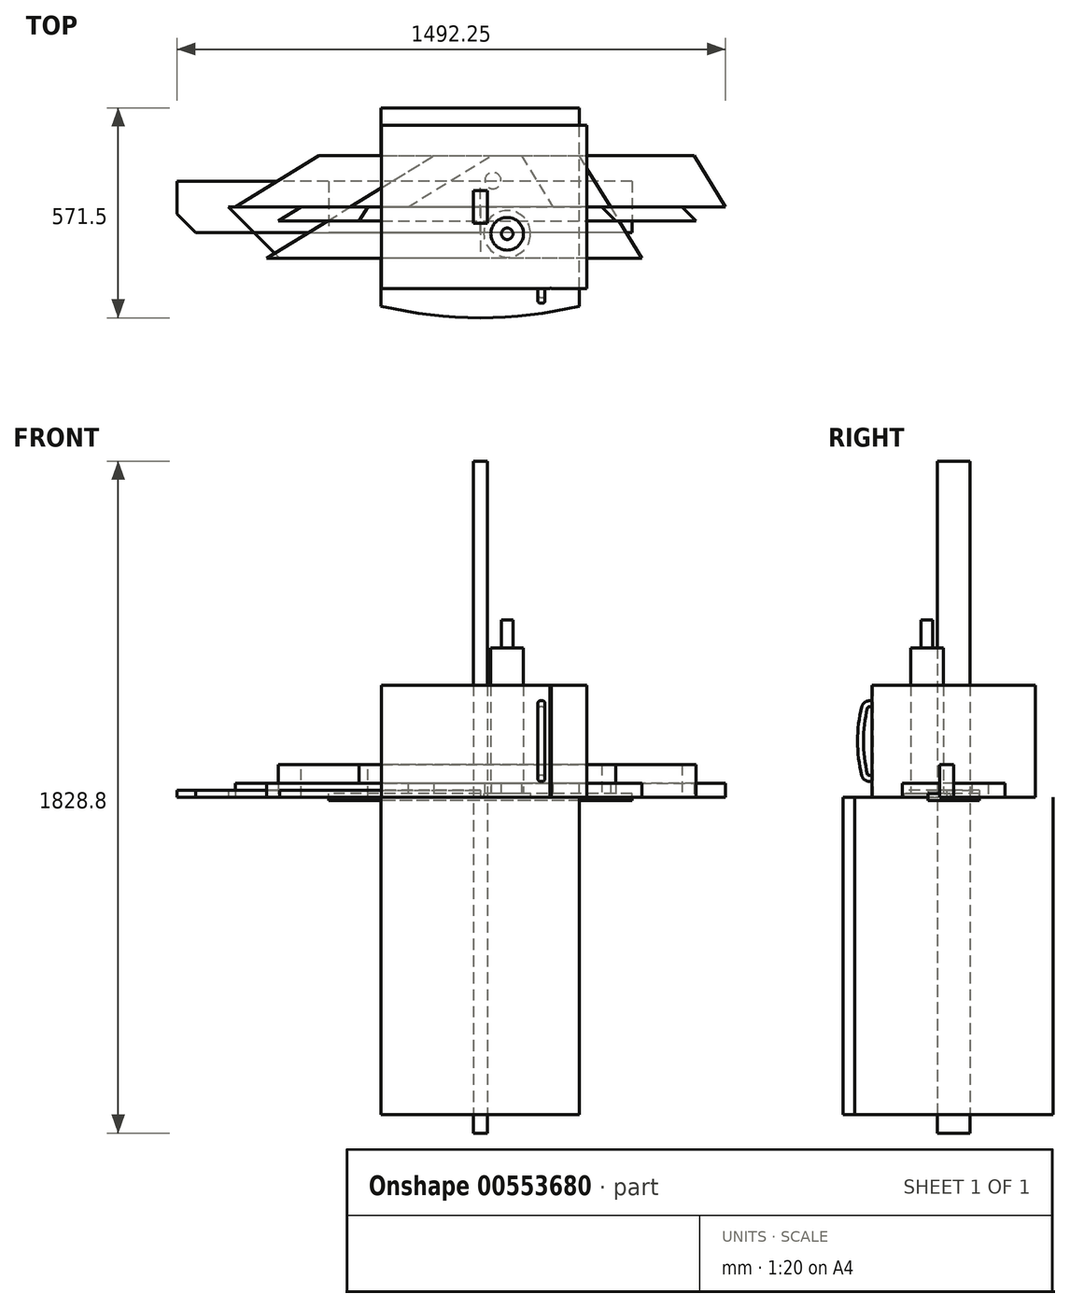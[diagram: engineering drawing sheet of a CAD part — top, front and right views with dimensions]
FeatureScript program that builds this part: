
annotation { "Feature Type Name" : "Feature", "Feature Type Description" : "" }
export const myFeature = defineFeature(function(context is Context, id is Id, definition is map)
    precondition{}
    {
        {
            var Q0;
            Q0=qCreatedBy(makeId("Top.planeOp"),FACE);
            var sketch = newSketch(context, id + "F0", { "sketchPlane" : qUnion([Q0])});
            skLineSegment(sketch, "E0.bottom", {"start": v(269.88, -269.88) * mm, "end": v(-269.88, -269.88) * mm});
            skLineSegment(sketch, "E0.top", {"start": v(269.88, 269.88) * mm, "end": v(-269.88, 269.88) * mm});
            skLineSegment(sketch, "E0.left", {"start": v(269.88, -269.88) * mm, "end": v(269.88, 269.88) * mm});
            skLineSegment(sketch, "E0.right", {"start": v(-269.88, -269.88) * mm, "end": v(-269.88, 269.88) * mm});
            skPoint(sketch, "E0.middle", {"position": v(0, 0) * mm});
            skArc(sketch, "E1", {"start": v(-269.88, -269.88) * mm, "mid": v(0, -301.62) * mm, "end": v(269.88, -269.87) * mm});
            skCircle(sketch, "E2", {"center": v(73.03, -73.03) * mm, "radius": 63.5 * mm});
            skCircle(sketch, "E3", {"center": v(73.03, -73.03) * mm, "radius": 44.45 * mm});
            skSolve(sketch);
        }
        {
            var Q0;
            Q0=makeQuery(id+"F0.imprint","IMPRINT",FACE,{"disambiguationData":[TD([[makeQuery(id+"F0.imprint","IMPRINT",EDGE,{"derivedFrom":sQuery(id+"F0.wireOp",EDGE,"E0.bottom")}),-1.0]])]});
            var Q1;
            Q1=makeQuery(id+"F0.imprint","IMPRINT",FACE,{"disambiguationData":[TD([[makeQuery(id+"F0.imprint","IMPRINT",EDGE,{"derivedFrom":sQuery(id+"F0.wireOp",EDGE,"E0.bottom")}),1.0]])]});
            var Q2;
            Q2=makeQuery(id+"F0.imprint","IMPRINT",FACE,{"disambiguationData":[TD([[makeQuery(id+"F0.imprint","IMPRINT",EDGE,{"derivedFrom":sQuery(id+"F0.wireOp",EDGE,"E2")}),1.0]])]});
            var Q3;
            Q3=makeQuery(id+"F0.imprint","IMPRINT",FACE,{"disambiguationData":[TD([[makeQuery(id+"F0.imprint","IMPRINT",EDGE,{"derivedFrom":sQuery(id+"F0.wireOp",EDGE,"E3")}),1.0]])]});
            extrude(context, id + "F1", {"entities" : qUnion([Q0, Q1, Q2, Q3]), "oppositeDirection" : true, "depth" : 863.6 * mm, "offsetDistance" : 25.4 * mm});
        }
        {
            var Q0;
            Q0=makeQuery(id+"F0.imprint","IMPRINT",FACE,{"disambiguationData":[TD([[makeQuery(id+"F0.imprint","IMPRINT",EDGE,{"derivedFrom":sQuery(id+"F0.wireOp",EDGE,"E3")}),1.0]])]});
            extrude(context, id + "F2", {"entities" : qUnion([Q0]), "operationType" : NewBodyOperationType.ADD, "depth" : 406.4 * mm, "offsetDistance" : 25.4 * mm});
        }
        {
            var Q0;
            Q0=makeQuery(id+"F0.imprint","IMPRINT",FACE,{"disambiguationData":[TD([[makeQuery(id+"F0.imprint","IMPRINT",EDGE,{"derivedFrom":sQuery(id+"F0.wireOp",EDGE,"E2")}),1.0]])]});
            extrude(context, id + "F3", {"entities" : qUnion([Q0]), "operationType" : NewBodyOperationType.ADD, "depth" : 9.52 * mm, "offsetDistance" : 25.4 * mm});
        }
        {
            var Q0;
            Q0=qCreatedBy(makeId("Right.planeOp"),FACE);
            var Q1;
            Q1=sQuery(id+"F0.wireOp",VERTEX,"E3.center");
            cPlane(context, id + "F4", {"entities" : qUnion([Q0, Q1]), "cplaneType" : CPlaneType.PLANE_POINT, "offset" : 114.3 * mm, "width" : 152.4 * mm, "height" : 152.4 * mm});
        }
        {
            var Q0;
            Q0=qCreatedBy(id+"F4.planeOp",FACE);
            var sketch = newSketch(context, id + "F5", { "sketchPlane" : qUnion([Q0])});
            skLineSegment(sketch, "E4", {"start": v(-117.48, 368.3) * mm, "end": v(-149.22, 368.3) * mm});
            skLineSegment(sketch, "E5", {"start": v(-149.22, 368.3) * mm, "end": v(-168.27, 349.25) * mm});
            skLineSegment(sketch, "E6", {"start": v(-168.27, 349.25) * mm, "end": v(-168.27, 336.55) * mm});
            skLineSegment(sketch, "E7", {"start": v(-117.48, 368.3) * mm, "end": v(-92.08, 368.3) * mm});
            skLineSegment(sketch, "E8", {"start": v(-117.48, 9.53) * mm, "end": v(-117.48, 406.4) * mm, "construction": true});
            skSolve(sketch);
        }
        {
            var Q0;
            Q0=makeQuery(id+"F2.opExtrude","CAP_FACE",FACE,{"disambiguationData":[OSD([sQuery(id+"F0.wireOp",EDGE,"E3")])],"isStart":false});
            var sketch = newSketch(context, id + "F6", { "sketchPlane" : qUnion([Q0])});
            skCircle(sketch, "E9", {"center": v(73.03, -73.03) * mm, "radius": 15.88 * mm});
            skSolve(sketch);
        }
        {
            var Q0;
            Q0=makeQuery(id+"F6.imprint","IMPRINT",FACE,{"disambiguationData":[TD([[makeQuery(id+"F6.imprint","IMPRINT",EDGE,{"derivedFrom":sQuery(id+"F6.wireOp",EDGE,"E9")}),1.0]])]});
            extrude(context, id + "F7", {"entities" : qUnion([Q0]), "operationType" : NewBodyOperationType.ADD, "depth" : 76.2 * mm, "offsetDistance" : 25.4 * mm});
        }
        {
            var Q0;
            Q0=qCreatedBy(makeId("Top.planeOp"),FACE);
            var sketch = newSketch(context, id + "F8", { "sketchPlane" : qUnion([Q0])});
            skLineSegment(sketch, "E10.bottom", {"start": v(289.8, -222.25) * mm, "end": v(-269, -222.25) * mm});
            skLineSegment(sketch, "E10.top", {"start": v(289.8, 222.25) * mm, "end": v(-269, 222.25) * mm});
            skLineSegment(sketch, "E10.left", {"start": v(289.8, -222.25) * mm, "end": v(289.8, 222.25) * mm});
            skLineSegment(sketch, "E10.right", {"start": v(-269, -222.25) * mm, "end": v(-269, 222.25) * mm});
            skPoint(sketch, "E10.middle", {"position": v(10.4, 0) * mm});
            skSolve(sketch);
        }
        {
            var Q0;
            Q0=makeQuery(id+"F8.imprint","IMPRINT",FACE,{"disambiguationData":[TD([[makeQuery(id+"F8.imprint","IMPRINT",EDGE,{"derivedFrom":sQuery(id+"F8.wireOp",EDGE,"E10.bottom")}),-1.0]])]});
            extrude(context, id + "F9", {"entities" : qUnion([Q0]), "depth" : 304.8 * mm, "offsetDistance" : 25.4 * mm});
        }
        {
            var Q0;
            Q0=makeQuery(id+"F9.opExtrude","SWEPT_FACE",FACE,{"disambiguationData":[OSD([sQuery(id+"F8.wireOp",EDGE,"E10.bottom")])]});
            var sketch = newSketch(context, id + "F10", { "sketchPlane" : qUnion([Q0])});
            skLineSegment(sketch, "E11", {"start": v(165.97, 254) * mm, "end": v(165.97, 50.8) * mm, "construction": true});
            skLineSegment(sketch, "E12.bottom", {"start": v(169.15, 246.06) * mm, "end": v(162.8, 246.06) * mm});
            skLineSegment(sketch, "E12.top", {"start": v(169.15, 261.94) * mm, "end": v(162.8, 261.94) * mm});
            skLineSegment(sketch, "E12.left", {"start": v(175.5, 252.41) * mm, "end": v(175.5, 255.59) * mm});
            skLineSegment(sketch, "E12.right", {"start": v(156.45, 252.41) * mm, "end": v(156.45, 255.59) * mm});
            skPoint(sketch, "E12.middle", {"position": v(165.97, 254) * mm});
            skPoint(sketch, "E13.visualSharp", {"position": v(156.45, 261.94) * mm});
            skArc(sketch, "E13.filletArc", {"start": v(162.8, 261.94) * mm, "mid": v(158.3, 260.08) * mm, "end": v(156.45, 255.59) * mm});
            skPoint(sketch, "E14.visualSharp", {"position": v(156.45, 246.06) * mm});
            skArc(sketch, "E14.filletArc", {"start": v(156.45, 252.41) * mm, "mid": v(158.3, 247.92) * mm, "end": v(162.8, 246.06) * mm});
            skPoint(sketch, "E15.visualSharp", {"position": v(175.5, 246.06) * mm});
            skArc(sketch, "E15.filletArc", {"start": v(169.15, 246.06) * mm, "mid": v(173.64, 247.92) * mm, "end": v(175.5, 252.41) * mm});
            skPoint(sketch, "E16.visualSharp", {"position": v(175.5, 261.94) * mm});
            skArc(sketch, "E16.filletArc", {"start": v(175.5, 255.59) * mm, "mid": v(173.64, 260.08) * mm, "end": v(169.15, 261.94) * mm});
            skSolve(sketch);
        }
        {
            var Q0;
            Q0=qCreatedBy(makeId("Right.planeOp"),FACE);
            cPlane(context, id + "F11", {"entities" : qUnion([Q0]), "cplaneType" : CPlaneType.OFFSET, "offset" : 161.92 * mm, "width" : 152.4 * mm, "height" : 152.4 * mm});
        }
        {
            var Q0;
            Q0=qCreatedBy(id+"F11.planeOp",FACE);
            var sketch = newSketch(context, id + "F12", { "sketchPlane" : qUnion([Q0])});
            skLineSegment(sketch, "E17.0", {"start": v(-222.25, 254) * mm, "end": v(-222.25, 50.8) * mm, "construction": true});
            skLineSegment(sketch, "E18", {"start": v(-222.25, 254) * mm, "end": v(-230.4, 254) * mm});
            skLineSegment(sketch, "E19", {"start": v(-230.4, 50.8) * mm, "end": v(-222.25, 50.8) * mm});
            skArc(sketch, "E20", {"start": v(-242.73, 244.37) * mm, "mid": v(-254, 152.4) * mm, "end": v(-242.73, 60.43) * mm});
            skPoint(sketch, "E21.visualSharp", {"position": v(-240.2, 254) * mm});
            skArc(sketch, "E21.filletArc", {"start": v(-230.4, 254) * mm, "mid": v(-238.23, 251.3) * mm, "end": v(-242.73, 244.37) * mm});
            skPoint(sketch, "E22.visualSharp", {"position": v(-240.2, 50.8) * mm});
            skArc(sketch, "E22.filletArc", {"start": v(-242.73, 60.43) * mm, "mid": v(-238.23, 53.5) * mm, "end": v(-230.4, 50.8) * mm});
            skSolve(sketch);
        }
        {
            var Q0;
            Q0=makeQuery(id+"F10.imprint","IMPRINT",FACE,{"disambiguationData":[TD([[makeQuery(id+"F10.imprint","IMPRINT",EDGE,{"derivedFrom":sQuery(id+"F10.wireOp",EDGE,"E12.bottom")}),-1.0]])]});
            var Q1;
            Q1=sQuery(id+"F12.wireOp",EDGE,"E18");
            var Q2;
            Q2=sQuery(id+"F12.wireOp",EDGE,"E21.filletArc");
            var Q3;
            Q3=sQuery(id+"F12.wireOp",EDGE,"E20");
            var Q4;
            Q4=sQuery(id+"F12.wireOp",EDGE,"E22.filletArc");
            var Q5;
            Q5=sQuery(id+"F12.wireOp",EDGE,"E19");
            sweep(context, id + "F13", {"operationType" : NewBodyOperationType.ADD, "profiles" : qUnion([Q0]), "path" : qUnion([Q1, Q2, Q3, Q4, Q5])});
        }
        {
            var Q0;
            Q0=makeQuery(id+"F9.opExtrude","SWEPT_FACE",FACE,{"disambiguationData":[OSD([sQuery(id+"F8.wireOp",EDGE,"E10.bottom")])]});
            var sketch = newSketch(context, id + "F14", { "sketchPlane" : qUnion([Q0])});
            skLineSegment(sketch, "E23", {"start": v(192.64, 304.8) * mm, "end": v(192.64, 0) * mm});
            skLineSegment(sketch, "E24", {"start": v(189.47, 304.8) * mm, "end": v(189.47, 0) * mm});
            skSolve(sketch);
        }
        {
            var Q0;
            {var subQ0=sQuery(id+"F14.wireOp",EDGE,"E23");Q0=makeQuery(id+"F14.imprint","IMPRINT",FACE,{"disambiguationData":[TD([[makeQuery(id+"F14.imprint","IMPRINT",EDGE,{"derivedFrom":subQ0}),-1.0]])]});}
            extrude(context, id + "F15", {"entities" : qUnion([Q0]), "operationType" : NewBodyOperationType.REMOVE, "oppositeDirection" : true, "depth" : 1.59 * mm, "offsetDistance" : 25.4 * mm});
        }
        {
            var Q0;
            Q0=qCreatedBy(makeId("Right.planeOp"),FACE);
            var sketch = newSketch(context, id + "F16", { "sketchPlane" : qUnion([Q0])});
            skLineSegment(sketch, "E25.bottom", {"start": v(69.85, -9.52) * mm, "end": v(-69.85, -9.53) * mm});
            skLineSegment(sketch, "E25.top", {"start": v(69.85, 9.53) * mm, "end": v(-69.85, 9.52) * mm});
            skLineSegment(sketch, "E25.left", {"start": v(69.85, -9.52) * mm, "end": v(69.85, 9.53) * mm});
            skLineSegment(sketch, "E25.right", {"start": v(-69.85, -9.53) * mm, "end": v(-69.85, 9.52) * mm});
            skPoint(sketch, "E25.middle", {"position": v(0, 0) * mm});
            skSolve(sketch);
        }
        {
            var Q0;
            Q0=makeQuery(id+"F16.imprint","IMPRINT",FACE,{"disambiguationData":[TD([[makeQuery(id+"F16.imprint","IMPRINT",EDGE,{"derivedFrom":sQuery(id+"F16.wireOp",EDGE,"E25.bottom")}),-1.0]])]});
            extrude(context, id + "F17", {"entities" : qUnion([Q0]), "endBound" : BoundingType.SYMMETRIC, "depth" : 825.5 * mm, "offsetDistance" : 25.4 * mm});
        }
        {
            var Q0;
            Q0=qCreatedBy(makeId("Top.planeOp"),FACE);
            var sketch = newSketch(context, id + "F18", { "sketchPlane" : qUnion([Q0])});
            skLineSegment(sketch, "E26", {"start": v(-774.7, -69.85) * mm, "end": v(0, -69.85) * mm});
            skLineSegment(sketch, "E27", {"start": v(0, -69.85) * mm, "end": v(0, 69.85) * mm});
            skLineSegment(sketch, "E28", {"start": v(0, 69.85) * mm, "end": v(-825.5, 69.85) * mm});
            skLineSegment(sketch, "E29", {"start": v(-825.5, 69.85) * mm, "end": v(-825.5, -19.05) * mm});
            skLineSegment(sketch, "E30", {"start": v(-825.5, -19.05) * mm, "end": v(-774.7, -69.85) * mm});
            skSolve(sketch);
        }
        {
            var Q0;
            Q0=makeQuery(id+"F18.imprint","IMPRINT",FACE,{"disambiguationData":[TD([[makeQuery(id+"F18.imprint","IMPRINT",EDGE,{"derivedFrom":sQuery(id+"F18.wireOp",EDGE,"E26")}),1.0]])]});
            extrude(context, id + "F19", {"entities" : qUnion([Q0]), "depth" : 19.05 * mm, "offsetDistance" : 25.4 * mm});
        }
        {
            var Q0;
            Q0=qCreatedBy(makeId("Top.planeOp"),FACE);
            var sketch = newSketch(context, id + "F20", { "sketchPlane" : qUnion([Q0])});
            skLineSegment(sketch, "E31", {"start": v(0, 0) * mm, "end": v(0, -139.7) * mm});
            skLineSegment(sketch, "E32", {"start": v(-685.8, 0) * mm, "end": v(0, 0) * mm});
            skLineSegment(sketch, "E33", {"start": v(0, -139.7) * mm, "end": v(-546.1, -139.7) * mm});
            skLineSegment(sketch, "E34", {"start": v(-546.1, -139.7) * mm, "end": v(-685.8, 0) * mm});
            skSolve(sketch);
        }
        {
            var Q0;
            Q0=makeQuery(id+"F20.imprint","IMPRINT",FACE,{"disambiguationData":[TD([[makeQuery(id+"F20.imprint","IMPRINT",EDGE,{"derivedFrom":sQuery(id+"F20.wireOp",EDGE,"E31")}),-1.0]])]});
            extrude(context, id + "F21", {"entities" : qUnion([Q0]), "depth" : 19.05 * mm, "offsetDistance" : 25.4 * mm});
        }
        {
            var Q0;
            Q0=qCreatedBy(makeId("Top.planeOp"),FACE);
            var sketch = newSketch(context, id + "F22", { "sketchPlane" : qUnion([Q0])});
            skLineSegment(sketch, "E35.bottom", {"start": v(19.05, -44.45) * mm, "end": v(-19.05, -44.45) * mm});
            skLineSegment(sketch, "E35.top", {"start": v(19.05, 44.45) * mm, "end": v(-19.05, 44.45) * mm});
            skLineSegment(sketch, "E35.left", {"start": v(19.05, -44.45) * mm, "end": v(19.05, 44.45) * mm});
            skLineSegment(sketch, "E35.right", {"start": v(-19.05, -44.45) * mm, "end": v(-19.05, 44.45) * mm});
            skPoint(sketch, "E35.middle", {"position": v(0, 0) * mm});
            skSolve(sketch);
        }
        {
            var Q0;
            Q0=makeQuery(id+"F22.imprint","IMPRINT",FACE,{"disambiguationData":[TD([[makeQuery(id+"F22.imprint","IMPRINT",EDGE,{"derivedFrom":sQuery(id+"F22.wireOp",EDGE,"E35.bottom")}),-1.0]])]});
            extrude(context, id + "F23", {"entities" : qUnion([Q0]), "endBound" : BoundingType.SYMMETRIC, "depth" : 1828.8 * mm, "offsetDistance" : 25.4 * mm});
        }
        {
            var Q0;
            Q0=qCreatedBy(makeId("Top.planeOp"),FACE);
            var sketch = newSketch(context, id + "F24", { "sketchPlane" : qUnion([Q0])});
            skLineSegment(sketch, "E36", {"start": v(666.75, 0) * mm, "end": v(-666.75, 0) * mm});
            skLineSegment(sketch, "E37", {"start": v(-666.75, 0) * mm, "end": v(-439.57, 139.7) * mm});
            skLineSegment(sketch, "E38", {"start": v(-439.57, 139.7) * mm, "end": v(581.05, 139.7) * mm});
            skLineSegment(sketch, "E39", {"start": v(581.05, 139.7) * mm, "end": v(666.75, 0) * mm});
            skLineSegment(sketch, "E40", {"start": v(666.75, 0) * mm, "end": v(301.49, 595.39) * mm, "construction": true});
            skLineSegment(sketch, "E41", {"start": v(301.49, 595.39) * mm, "end": v(-666.75, 0) * mm, "construction": true});
            skSolve(sketch);
        }
        {
            var Q0;
            Q0=makeQuery(id+"F24.imprint","IMPRINT",FACE,{"disambiguationData":[TD([[makeQuery(id+"F24.imprint","IMPRINT",EDGE,{"derivedFrom":sQuery(id+"F24.wireOp",EDGE,"E36")}),-1.0]])]});
            extrude(context, id + "F25", {"entities" : qUnion([Q0]), "depth" : 38.1 * mm, "offsetDistance" : 25.4 * mm});
        }
        {
            var Q0;
            Q0=qCreatedBy(makeId("Top.planeOp"),FACE);
            var sketch = newSketch(context, id + "F26", { "sketchPlane" : qUnion([Q0])});
            skLineSegment(sketch, "E42", {"start": v(-549.28, 0) * mm, "end": v(-549.28, -38.1) * mm});
            skLineSegment(sketch, "E43", {"start": v(-549.28, -38.1) * mm, "end": v(587.38, -38.1) * mm});
            skLineSegment(sketch, "E44", {"start": v(587.38, -38.1) * mm, "end": v(549.28, 0) * mm});
            skLineSegment(sketch, "E45", {"start": v(549.28, 0) * mm, "end": v(-549.28, 0) * mm});
            skSolve(sketch);
        }
        {
            var Q0;
            Q0=makeQuery(id+"F26.imprint","IMPRINT",FACE,{"disambiguationData":[TD([[makeQuery(id+"F26.imprint","IMPRINT",EDGE,{"derivedFrom":sQuery(id+"F26.wireOp",EDGE,"E42")}),1.0]])]});
            extrude(context, id + "F27", {"entities" : qUnion([Q0]), "depth" : 88.9 * mm, "offsetDistance" : 25.4 * mm});
        }
        {
            var Q0;
            Q0=qCreatedBy(makeId("Top.planeOp"),FACE);
            var sketch = newSketch(context, id + "F28", { "sketchPlane" : qUnion([Q0])});
            skLineSegment(sketch, "E46", {"start": v(-330.2, 0) * mm, "end": v(-330.2, -38.1) * mm});
            skLineSegment(sketch, "E47", {"start": v(-330.2, -38.1) * mm, "end": v(368.3, -38.1) * mm});
            skLineSegment(sketch, "E48", {"start": v(368.3, -38.1) * mm, "end": v(330.2, 0) * mm});
            skLineSegment(sketch, "E49", {"start": v(330.2, 0) * mm, "end": v(-330.2, 0) * mm});
            skSolve(sketch);
        }
        {
            var Q0;
            Q0=makeQuery(id+"F28.imprint","IMPRINT",FACE,{"disambiguationData":[TD([[makeQuery(id+"F28.imprint","IMPRINT",EDGE,{"derivedFrom":sQuery(id+"F28.wireOp",EDGE,"E46")}),1.0]])]});
            extrude(context, id + "F29", {"entities" : qUnion([Q0]), "depth" : 88.9 * mm, "offsetDistance" : 25.4 * mm});
        }
        {
            var Q0;
            Q0=makeQuery(id+"F29.opExtrude","SWEPT_EDGE",EDGE,{"disambiguationData":[OSD([sQuery(id+"F28.wireOp",EDGE,"E46"),sQuery(id+"F28.wireOp",EDGE,"E49")])]});
            chamfer(context, id + "F30", {"entities" : qUnion([Q0]), "chamferType" : ChamferType.OFFSET_ANGLE, "width" : 38.1 * mm, "oppositeDirection" : false, "angle" : 32 * degree, "tangentPropagation" : true});
        }
        {
            var Q0;
            Q0=makeQuery(id+"F27.opExtrude","SWEPT_EDGE",EDGE,{"disambiguationData":[OSD([sQuery(id+"F26.wireOp",EDGE,"E42"),sQuery(id+"F26.wireOp",EDGE,"E45")])]});
            chamfer(context, id + "F31", {"entities" : qUnion([Q0]), "chamferType" : ChamferType.OFFSET_ANGLE, "width" : 38.1 * mm, "oppositeDirection" : false, "angle" : 58.5 * degree, "tangentPropagation" : true});
        }
        {
            var Q0;
            Q0=qCreatedBy(makeId("Top.planeOp"),FACE);
            var sketch = newSketch(context, id + "F32", { "sketchPlane" : qUnion([Q0])});
            skLineSegment(sketch, "E50", {"start": v(439.57, -139.7) * mm, "end": v(-581.05, -139.7) * mm});
            skLineSegment(sketch, "E51", {"start": v(-581.05, -139.7) * mm, "end": v(-353.87, 0) * mm});
            skLineSegment(sketch, "E52", {"start": v(-353.87, 0) * mm, "end": v(353.87, 0) * mm});
            skLineSegment(sketch, "E53", {"start": v(353.87, 0) * mm, "end": v(439.57, -139.7) * mm});
            skSolve(sketch);
        }
        {
            var Q0;
            Q0=makeQuery(id+"F32.imprint","IMPRINT",FACE,{"disambiguationData":[TD([[makeQuery(id+"F32.imprint","IMPRINT",EDGE,{"derivedFrom":sQuery(id+"F32.wireOp",EDGE,"E50")}),-1.0]])]});
            extrude(context, id + "F33", {"entities" : qUnion([Q0]), "depth" : 38.1 * mm, "offsetDistance" : 25.4 * mm});
        }
        {
            var Q0;
            Q0=qCreatedBy(makeId("Top.planeOp"),FACE);
            var sketch = newSketch(context, id + "F34", { "sketchPlane" : qUnion([Q0])});
            skLineSegment(sketch, "E54", {"start": v(353.87, 0) * mm, "end": v(-353.87, 0) * mm});
            skLineSegment(sketch, "E55", {"start": v(-353.87, 0) * mm, "end": v(-126.69, 139.7) * mm});
            skLineSegment(sketch, "E56", {"start": v(-126.69, 139.7) * mm, "end": v(268.17, 139.7) * mm});
            skLineSegment(sketch, "E57", {"start": v(268.17, 139.7) * mm, "end": v(353.87, 0) * mm});
            skSolve(sketch);
        }
        {
            var Q0;
            Q0 = qSketchRegion(id + "F34", true);
            extrude(context, id + "F35", {"entities" : qUnion([Q0]), "depth" : 38.1 * mm, "offsetDistance" : 25.4 * mm});
        }
        {
            var Q0;
            Q0=qCreatedBy(makeId("Top.planeOp"),FACE);
            var sketch = newSketch(context, id + "F36", { "sketchPlane" : qUnion([Q0])});
            skLineSegment(sketch, "E58", {"start": v(197.43, 0) * mm, "end": v(-197.43, 0) * mm});
            skLineSegment(sketch, "E59", {"start": v(-197.43, 0) * mm, "end": v(29.75, 139.7) * mm});
            skLineSegment(sketch, "E60", {"start": v(29.75, 139.7) * mm, "end": v(111.73, 139.7) * mm});
            skLineSegment(sketch, "E61", {"start": v(111.73, 139.7) * mm, "end": v(197.43, 0) * mm});
            skCircle(sketch, "E62", {"center": v(34.27, 71.66) * mm, "radius": 22.23 * mm});
            skSolve(sketch);
        }
        {
            var Q0;
            Q0=makeQuery(id+"F36.imprint","IMPRINT",FACE,{"disambiguationData":[TD([[makeQuery(id+"F36.imprint","IMPRINT",EDGE,{"derivedFrom":sQuery(id+"F36.wireOp",EDGE,"E58")}),-1.0]])]});
            extrude(context, id + "F37", {"entities" : qUnion([Q0]), "depth" : 38.1 * mm, "offsetDistance" : 25.4 * mm});
        }
    });
